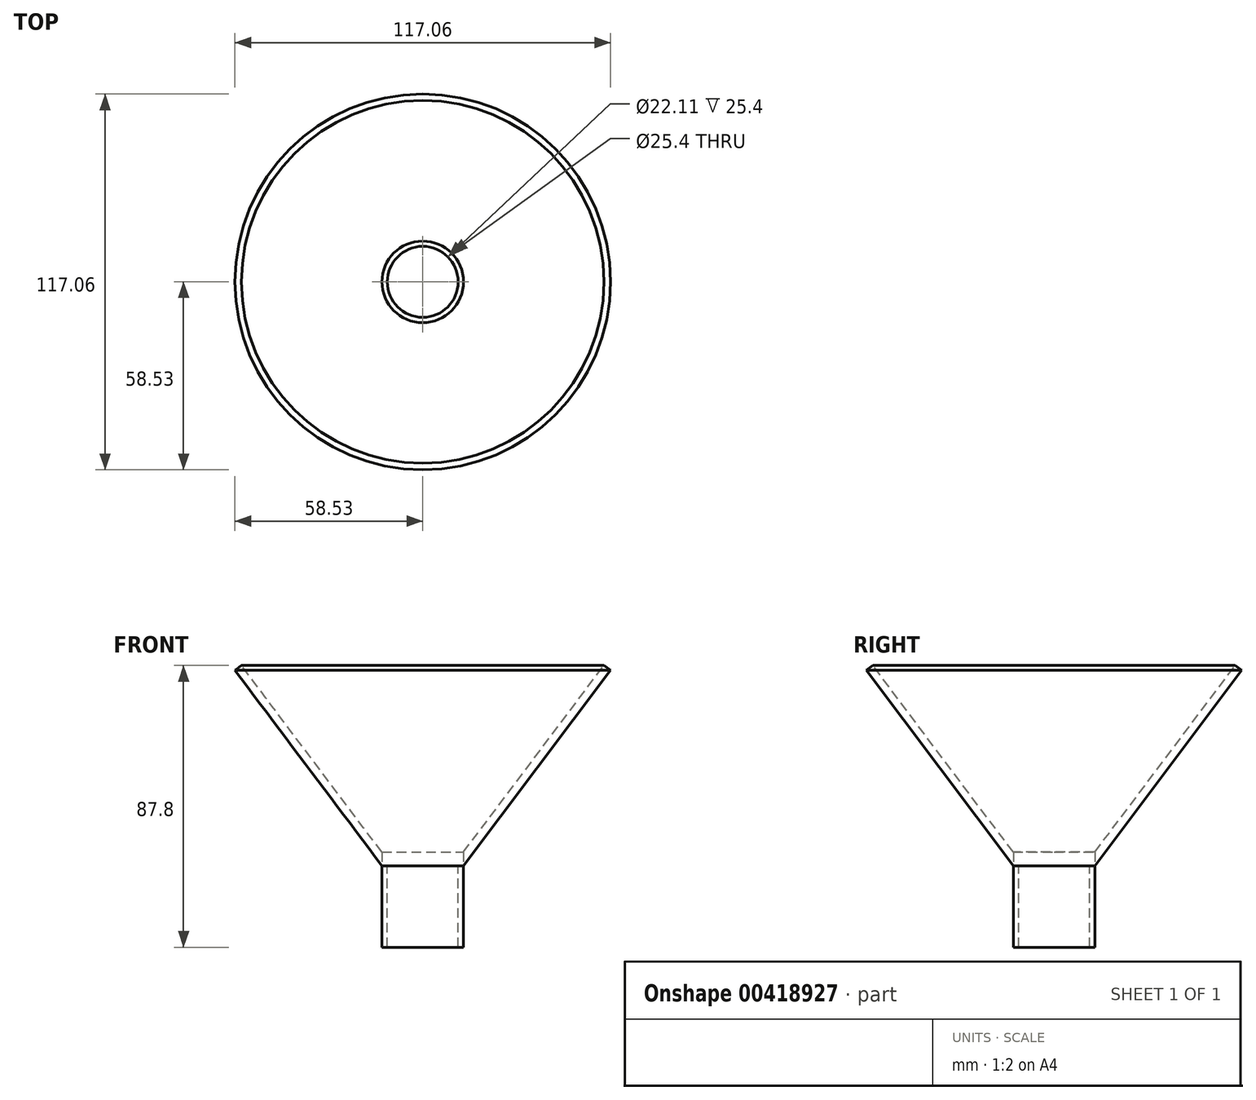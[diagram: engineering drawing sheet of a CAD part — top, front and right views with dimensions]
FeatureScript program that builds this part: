
annotation { "Feature Type Name" : "Feature", "Feature Type Description" : "" }
export const myFeature = defineFeature(function(context is Context, id is Id, definition is map)
    precondition{}
    {
        {
            var Q0;
            Q0=qCreatedBy(makeId("Front.planeOp"),FACE);
            var sketch = newSketch(context, id + "F0", { "sketchPlane" : qUnion([Q0])});
            skLineSegment(sketch, "E0", {"start": v(0, -25.4) * mm, "end": v(0, 0) * mm});
            skLineSegment(sketch, "E1", {"start": v(0, 0) * mm, "end": v(45.83, 60.88) * mm});
            skLineSegment(sketch, "E2", {"start": v(45.83, 60.88) * mm, "end": v(43.8, 62.4) * mm});
            skLineSegment(sketch, "E3", {"start": v(43.8, 62.4) * mm, "end": v(0, 4.22) * mm});
            skLineSegment(sketch, "E4", {"start": v(0, 4.22) * mm, "end": v(0, 0) * mm});
            skLineSegment(sketch, "E5", {"start": v(0, -25.4) * mm, "end": v(-12.7, -25.4) * mm});
            skLineSegment(sketch, "E6", {"start": v(-12.7, -25.4) * mm, "end": v(-12.7, 0) * mm});
            skLineSegment(sketch, "E7", {"start": v(-12.7, 0) * mm, "end": v(0, 0) * mm});
            skSolve(sketch);
        }
        {
            var Q0;
            Q0=makeQuery(id+"F0.imprint","IMPRINT",FACE,{"disambiguationData":[TD([[makeQuery(id+"F0.imprint","IMPRINT",EDGE,{"derivedFrom":sQuery(id+"F0.wireOp",EDGE,"E1")}),1.0]])]});
            var Q1;
            Q1=makeQuery(id+"F0.imprint","IMPRINT",FACE,{"disambiguationData":[TD([[makeQuery(id+"F0.imprint","IMPRINT",EDGE,{"derivedFrom":sQuery(id+"F0.wireOp",EDGE,"E0")}),1.0]])]});
            var Q2;
            Q2=sQuery(id+"F0.wireOp",EDGE,"E6");
            revolve(context, id + "F1", {"entities" : qUnion([Q0, Q1]), "axis" : qUnion([Q2]), "revolveType" : RevolveType.FULL});
        }
        {
            var Q0;
            Q0=makeQuery(id+"F1.opRevolve","SWEPT_FACE",FACE,{"disambiguationData":[OSD([sQuery(id+"F0.wireOp",EDGE,"E7")])]});
            var sketch = newSketch(context, id + "F2", { "sketchPlane" : qUnion([Q0])});
            skCircle(sketch, "E8", {"center": v(-12.7, 0) * mm, "radius": 11.06 * mm});
            skSolve(sketch);
        }
        {
            var Q0;
            Q0=makeQuery(id+"F2.imprint","IMPRINT",FACE,{"disambiguationData":[TD([[makeQuery(id+"F2.imprint","IMPRINT",EDGE,{"derivedFrom":sQuery(id+"F2.wireOp",EDGE,"E8")}),1.0]])]});
            extrude(context, id + "F3", {"entities" : qUnion([Q0]), "operationType" : NewBodyOperationType.REMOVE, "oppositeDirection" : true, "depth" : 25.4 * mm});
        }
    });
